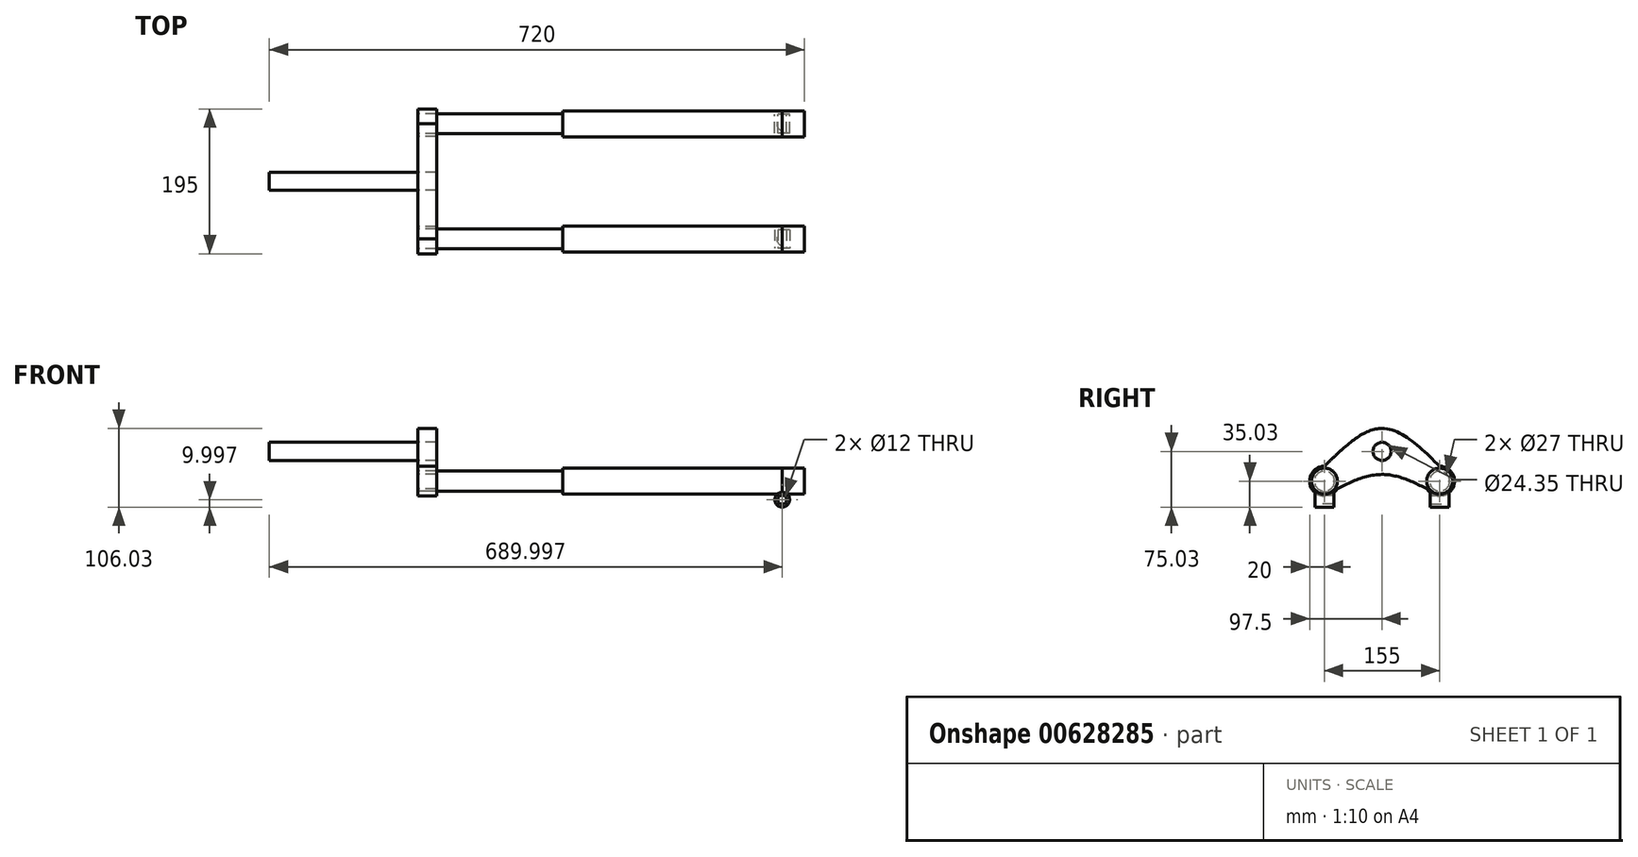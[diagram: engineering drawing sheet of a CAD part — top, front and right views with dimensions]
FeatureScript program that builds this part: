
annotation { "Feature Type Name" : "Feature", "Feature Type Description" : "" }
export const myFeature = defineFeature(function(context is Context, id is Id, definition is map)
    precondition{}
    {
        {
            var Q0;
            Q0=qCreatedBy(makeId("Right.planeOp"),FACE);
            var sketch = newSketch(context, id + "F0", { "sketchPlane" : qUnion([Q0])});
            skLineSegment(sketch, "E0", {"start": v(0, 0) * mm, "end": v(-77.5, 0) * mm, "construction": true});
            skLineSegment(sketch, "E1", {"start": v(0, 0) * mm, "end": v(77.5, 0) * mm, "construction": true});
            skLineSegment(sketch, "E2.0", {"start": v(0, 40) * mm, "end": v(77.5, 40) * mm, "construction": true});
            skLineSegment(sketch, "E2.1", {"start": v(0, 40) * mm, "end": v(-77.5, 40) * mm, "construction": true});
            skLineSegment(sketch, "E3", {"start": v(0, 0) * mm, "end": v(0, 40) * mm, "construction": true});
            skLineSegment(sketch, "E4.0", {"start": v(77.5, 0) * mm, "end": v(77.5, 40) * mm, "construction": true});
            skLineSegment(sketch, "E5.0", {"start": v(-77.5, 0) * mm, "end": v(-77.5, 40) * mm, "construction": true});
            skCircle(sketch, "E6", {"center": v(-77.5, 0) * mm, "radius": 13.5 * mm});
            skCircle(sketch, "E7", {"center": v(77.5, 0) * mm, "radius": 13.5 * mm});
            skCircle(sketch, "E8", {"center": v(77.5, 0) * mm, "radius": 20 * mm});
            skCircle(sketch, "E9", {"center": v(-77.5, 0) * mm, "radius": 20 * mm});
            skCircle(sketch, "E10", {"center": v(0, 40) * mm, "radius": 12.18 * mm});
            skCircle(sketch, "E11", {"center": v(0, 40) * mm, "radius": 31 * mm});
            skLineSegment(sketch, "E12.MirrorCS", {"start": v(77.5, 0) * mm, "end": v(77.5, -40) * mm, "construction": true});
            skLineSegment(sketch, "E13.MirrorCS", {"start": v(-77.5, 0) * mm, "end": v(-77.5, -40) * mm, "construction": true});
            skLineSegment(sketch, "E14.0", {"start": v(5, 45) * mm, "end": v(-77.5, 45) * mm});
            skLineSegment(sketch, "E14.1", {"start": v(5, 0) * mm, "end": v(5, 45) * mm});
            skLineSegment(sketch, "E15", {"start": v(0, 40) * mm, "end": v(0, 74.35) * mm, "construction": true});
            skPoint(sketch, "E16", {"position": v(0, 71) * mm});
            skPoint(sketch, "E17", {"position": v(77.5, 20) * mm});
            skPoint(sketch, "E18", {"position": v(-77.5, 20) * mm});
            skFitSpline(sketch, "E19", {"points": [v(77.5, 20) * mm, v(0, 71) * mm, v(-77.5, 20) * mm], "startDerivative": vector(-155, 153) * mm, "endDerivative": vector(-155, -153) * mm});
            skPoint(sketch, "E20", {"position": v(77.5, -20) * mm});
            skPoint(sketch, "E21", {"position": v(0, 9) * mm});
            skPoint(sketch, "E22", {"position": v(-77.5, -20) * mm});
            skFitSpline(sketch, "E23", {"points": [v(77.5, -20) * mm, v(0, 9) * mm, v(-77.5, -20) * mm], "startDerivative": vector(-155, 87) * mm, "endDerivative": vector(-155, -87) * mm});
            skSolve(sketch);
        }
        {
            var Q0;
            Q0=makeQuery(id+"F0.imprint","IMPRINT",FACE,{"disambiguationData":[TD([[makeQuery(id+"F0.imprint","IMPRINT",EDGE,{"derivedFrom":sQuery(id+"F0.wireOp",EDGE,"E7")}),1.0]])]});
            var Q1;
            Q1=makeQuery(id+"F0.imprint","IMPRINT",FACE,{"disambiguationData":[TD([[makeQuery(id+"F0.imprint","IMPRINT",EDGE,{"derivedFrom":sQuery(id+"F0.wireOp",EDGE,"E6")}),1.0]])]});
            extrude(context, id + "F1", {"entities" : qUnion([Q0, Q1]), "depth" : 195 * mm, "offsetDistance" : 25 * mm});
        }
        {
            var Q0;
            Q0 = qSketchRegion(id + "F0", true);
            extrude(context, id + "F2", {"entities" : qUnion([Q0]), "depth" : 25 * mm, "offsetDistance" : 25 * mm});
        }
        {
            var Q0;
            {var subQ0=sQuery(id+"F0.wireOp",EDGE,"E14.0");var subQ1=sQuery(id+"F0.wireOp",EDGE,"E10");var subQ2=makeQuery(id+"F0.imprint","INTERSECT",VERTEX,{"derivedFrom":[subQ1,subQ0]});Q0=makeQuery(id+"F0.imprint","IMPRINT",FACE,{"disambiguationData":[TD([[makeQuery(id+"F0.imprint","IMPRINT",EDGE,{"disambiguationData":[TD([[subQ2,-1.0]])],"derivedFrom":subQ1}),1.0]])]});}
            var Q1;
            {var subQ0=sQuery(id+"F0.wireOp",EDGE,"E14.0");var subQ1=sQuery(id+"F0.wireOp",EDGE,"E10");var subQ2=makeQuery(id+"F0.imprint","INTERSECT",VERTEX,{"derivedFrom":[subQ1,subQ0]});Q1=makeQuery(id+"F0.imprint","IMPRINT",FACE,{"disambiguationData":[TD([[makeQuery(id+"F0.imprint","IMPRINT",EDGE,{"disambiguationData":[TD([[subQ2,1.0]])],"derivedFrom":subQ1}),1.0]])]});}
            extrude(context, id + "F3", {"entities" : qUnion([Q0, Q1]), "oppositeDirection" : true, "depth" : 200 * mm, "offsetDistance" : 25 * mm});
        }
        {
            var Q0;
            Q0=makeQuery(id+"F1.opExtrude","CAP_FACE",FACE,{"disambiguationData":[OSD([sQuery(id+"F0.wireOp",EDGE,"E7")])],"isStart":false});
            var sketch = newSketch(context, id + "F4", { "sketchPlane" : qUnion([Q0])});
            skCircle(sketch, "E24", {"center": v(77.5, 0) * mm, "radius": 17.5 * mm});
            skSolve(sketch);
        }
        {
            var Q0;
            Q0=makeQuery(id+"F1.opExtrude","CAP_FACE",FACE,{"disambiguationData":[OSD([sQuery(id+"F0.wireOp",EDGE,"E6")])],"isStart":false});
            var sketch = newSketch(context, id + "F5", { "sketchPlane" : qUnion([Q0])});
            skCircle(sketch, "E25", {"center": v(-77.5, 0) * mm, "radius": 17.5 * mm});
            skSolve(sketch);
        }
        {
            var Q0;
            Q0=makeQuery(id+"F3.opExtrude","CAP_FACE",FACE,{"disambiguationData":[OSD([sQuery(id+"F0.wireOp",EDGE,"E10")])],"isStart":true});
            extrude(context, id + "F6", {"entities" : qUnion([Q0]), "depth" : 25 * mm, "offsetDistance" : 25 * mm});
        }
        {
            var Q0;
            Q0=makeQuery(id+"F5.imprint","IMPRINT",FACE,{"disambiguationData":[TD([[makeQuery(id+"F5.imprint","IMPRINT",EDGE,{"derivedFrom":sQuery(id+"F5.wireOp",EDGE,"E25")}),1.0]])]});
            var Q1;
            Q1=makeQuery(id+"F4.imprint","IMPRINT",FACE,{"disambiguationData":[TD([[makeQuery(id+"F4.imprint","IMPRINT",EDGE,{"derivedFrom":sQuery(id+"F4.wireOp",EDGE,"E24")}),1.0]])]});
            var Q2;
            Q2=makeQuery(id+"F5.imprint","IMPRINT",FACE,{"disambiguationData":[TD([[makeQuery(id+"F5.imprint","IMPRINT",EDGE,{"derivedFrom":makeQuery(id+"F1.opExtrude","CAP_EDGE",EDGE,{"disambiguationData":[OSD([sQuery(id+"F0.wireOp",EDGE,"E6")])],"isStart":false})}),1.0]])]});
            var Q3;
            Q3=makeQuery(id+"F4.imprint","IMPRINT",FACE,{"disambiguationData":[TD([[makeQuery(id+"F4.imprint","IMPRINT",EDGE,{"derivedFrom":makeQuery(id+"F1.opExtrude","CAP_EDGE",EDGE,{"disambiguationData":[OSD([sQuery(id+"F0.wireOp",EDGE,"E7")])],"isStart":false})}),1.0]])]});
            extrude(context, id + "F7", {"entities" : qUnion([Q0, Q1, Q2, Q3]), "depth" : 295 * mm, "offsetDistance" : 25 * mm});
        }
        {
            var Q0;
            Q0=makeQuery(id+"F7.opExtrude","CAP_FACE",FACE,{"disambiguationData":[OSD([sQuery(id+"F5.wireOp",EDGE,"E25")])],"isStart":false});
            var sketch = newSketch(context, id + "F8", { "sketchPlane" : qUnion([Q0])});
            skLineSegment(sketch, "E26", {"start": v(109.4, 0) * mm, "end": v(-105.9, 0) * mm, "construction": true});
            skLineSegment(sketch, "E27.0", {"start": v(78.55, -17.5) * mm, "end": v(-77.5, -17.5) * mm, "construction": true});
            skArc(sketch, "E28.0", {"start": v(32.34, -46.42) * mm, "mid": v(132.3, -34.52) * mm, "end": v(99.87, 60.78) * mm, "construction": true});
            skFitSpline(sketch, "E28.1", {"points": [v(-55.59, -59.04) * mm, v(-52.36, -57.22) * mm, v(-46.07, -53.7) * mm, v(-37.18, -48.87) * mm, v(-28.88, -44.65) * mm, v(-21.25, -41.18) * mm, v(-15.56, -39) * mm, v(-11.47, -37.7) * mm, v(-8.66, -36.93) * mm, v(-6.1, -36.38) * mm, v(-4.19, -36.07) * mm, v(-2.79, -35.9) * mm, v(-1.8, -35.82) * mm, v(-1.02, -35.78) * mm, v(-0.43, -35.77) * mm, v(0, -35.76) * mm, v(0.43, -35.77) * mm, v(1.02, -35.78) * mm, v(1.8, -35.82) * mm, v(2.79, -35.9) * mm, v(4.19, -36.07) * mm, v(6.1, -36.38) * mm, v(8.66, -36.93) * mm, v(11.47, -37.7) * mm, v(15.56, -39) * mm, v(21.25, -41.18) * mm, v(28.88, -44.65) * mm, v(37.18, -48.87) * mm, v(46.07, -53.7) * mm, v(52.36, -57.22) * mm, v(55.59, -59.04) * mm], "construction": true});
            skArc(sketch, "E28.2", {"start": v(-99.87, 60.78) * mm, "mid": v(-132.3, -34.52) * mm, "end": v(-32.34, -46.42) * mm, "construction": true});
            skFitSpline(sketch, "E28.3", {"points": [v(108.95, 51.86) * mm, v(105.72, 55.05) * mm, v(99.1, 61.58) * mm, v(88.64, 71.6) * mm, v(77.54, 81.54) * mm, v(67.58, 89.55) * mm, v(59, 95.64) * mm, v(52.21, 100) * mm, v(44.97, 104.08) * mm, v(37.22, 107.8) * mm, v(30.27, 110.5) * mm, v(24.38, 112.32) * mm, v(19.8, 113.5) * mm, v(15.07, 114.47) * mm, v(11, 115.08) * mm, v(7.67, 115.43) * mm, v(5.14, 115.62) * mm, v(3.01, 115.72) * mm, v(1.3, 115.76) * mm, v(0, 115.77) * mm, v(-1.3, 115.76) * mm, v(-3.01, 115.72) * mm, v(-5.14, 115.62) * mm, v(-7.67, 115.43) * mm, v(-11, 115.08) * mm, v(-15.07, 114.47) * mm, v(-19.8, 113.5) * mm, v(-24.38, 112.32) * mm, v(-30.27, 110.5) * mm, v(-37.22, 107.8) * mm, v(-44.97, 104.08) * mm, v(-52.21, 100) * mm, v(-59, 95.64) * mm, v(-67.58, 89.55) * mm, v(-77.54, 81.54) * mm, v(-88.64, 71.6) * mm, v(-99.1, 61.58) * mm, v(-105.72, 55.05) * mm, v(-108.95, 51.86) * mm], "construction": true});
            skPoint(sketch, "E29.orphan", {"position": v(78.55, 0) * mm});
            skLineSegment(sketch, "E30.0", {"start": v(109.4, 30) * mm, "end": v(-105.9, 30) * mm, "construction": true});
            skSolve(sketch);
        }
        {
            var Q0;
            Q0=makeQuery(id+"F7.opExtrude","CAP_FACE",FACE,{"disambiguationData":[OSD([sQuery(id+"F4.wireOp",EDGE,"E24")])],"isStart":false});
            var sketch = newSketch(context, id + "F9", { "sketchPlane" : qUnion([Q0])});
            skCircle(sketch, "E31", {"center": v(77.5, 0) * mm, "radius": 25 * mm});
            skCircle(sketch, "E32", {"center": v(-77.43, 0) * mm, "radius": 25 * mm});
            skLineSegment(sketch, "E33", {"start": v(-77.43, 0) * mm, "end": v(-77.43, -25) * mm, "construction": true});
            skLineSegment(sketch, "E34", {"start": v(77.5, 0) * mm, "end": v(77.5, -25) * mm, "construction": true});
            skSolve(sketch);
        }
        {
            var Q0;
            Q0=sQuery(id+"F9.wireOp",EDGE,"E34");
            cPlane(context, id + "F10", {"entities" : qUnion([Q0]), "cplaneType" : CPlaneType.LINE_ANGLE, "offset" : 25 * mm, "angle" : 270 * degree, "width" : 150 * mm, "height" : 150 * mm});
        }
        {
            var Q0;
            Q0=qCreatedBy(id+"F10.planeOp",FACE);
            var sketch = newSketch(context, id + "F11", { "sketchPlane" : qUnion([Q0])});
            skCircle(sketch, "E35", {"center": v(490, -25.03) * mm, "radius": 6 * mm});
            skCircle(sketch, "E36", {"center": v(490, -25.03) * mm, "radius": 10 * mm});
            skSolve(sketch);
        }
        {
            var Q0;
            Q0=makeQuery(id+"F11.imprint","IMPRINT",FACE,{"disambiguationData":[TD([[makeQuery(id+"F11.imprint","IMPRINT",EDGE,{"derivedFrom":sQuery(id+"F11.wireOp",EDGE,"E35")}),-1.0]])]});
            extrude(context, id + "F12", {"entities" : qUnion([Q0]), "depth" : 12.5 * mm, "offsetDistance" : 25 * mm});
        }
        {
            var Q0;
            Q0=makeQuery(id+"F12.opExtrude","CAP_FACE",FACE,{"disambiguationData":[OSD([sQuery(id+"F11.wireOp",EDGE,"E35"),sQuery(id+"F11.wireOp",EDGE,"E36")])],"isStart":true});
            extrude(context, id + "F13", {"entities" : qUnion([Q0]), "depth" : 12.5 * mm, "offsetDistance" : 25 * mm});
        }
        {
            var Q0;
            Q0=makeQuery(id+"F13.opExtrude","SWEPT_BODY",BODY,{"disambiguationData":[OSD([sQuery(id+"F11.wireOp",EDGE,"E35"),sQuery(id+"F11.wireOp",EDGE,"E36")])]});
            var Q1;
            Q1=makeQuery(id+"F12.opExtrude","SWEPT_BODY",BODY,{"disambiguationData":[OSD([sQuery(id+"F11.wireOp",EDGE,"E35"),sQuery(id+"F11.wireOp",EDGE,"E36")])]});
            var Q2;
            Q2=qCreatedBy(makeId("Front.planeOp"),FACE);
            mirror(context, id + "F14", {"operationType" : NewBodyOperationType.ADD, "entities" : qUnion([Q0, Q1]), "mirrorPlane" : qUnion([Q2])});
        }
        {
            var Q0;
            Q0=makeQuery(id+"F9.imprint","IMPRINT",FACE,{"disambiguationData":[TD([[makeQuery(id+"F9.imprint","IMPRINT",EDGE,{"derivedFrom":makeQuery(id+"F7.opExtrude","CAP_EDGE",EDGE,{"disambiguationData":[OSD([sQuery(id+"F4.wireOp",EDGE,"E24")])],"isStart":false})}),1.0]])]});
            var Q1;
            Q1=makeQuery(id+"F8.imprint","IMPRINT",FACE,{"disambiguationData":[TD([[makeQuery(id+"F8.imprint","IMPRINT",EDGE,{"derivedFrom":makeQuery(id+"F7.opExtrude","CAP_EDGE",EDGE,{"disambiguationData":[OSD([sQuery(id+"F5.wireOp",EDGE,"E25")])],"isStart":false})}),1.0]])]});
            extrude(context, id + "F15", {"entities" : qUnion([Q0, Q1]), "depth" : 30 * mm, "offsetDistance" : 25 * mm});
        }
    });
